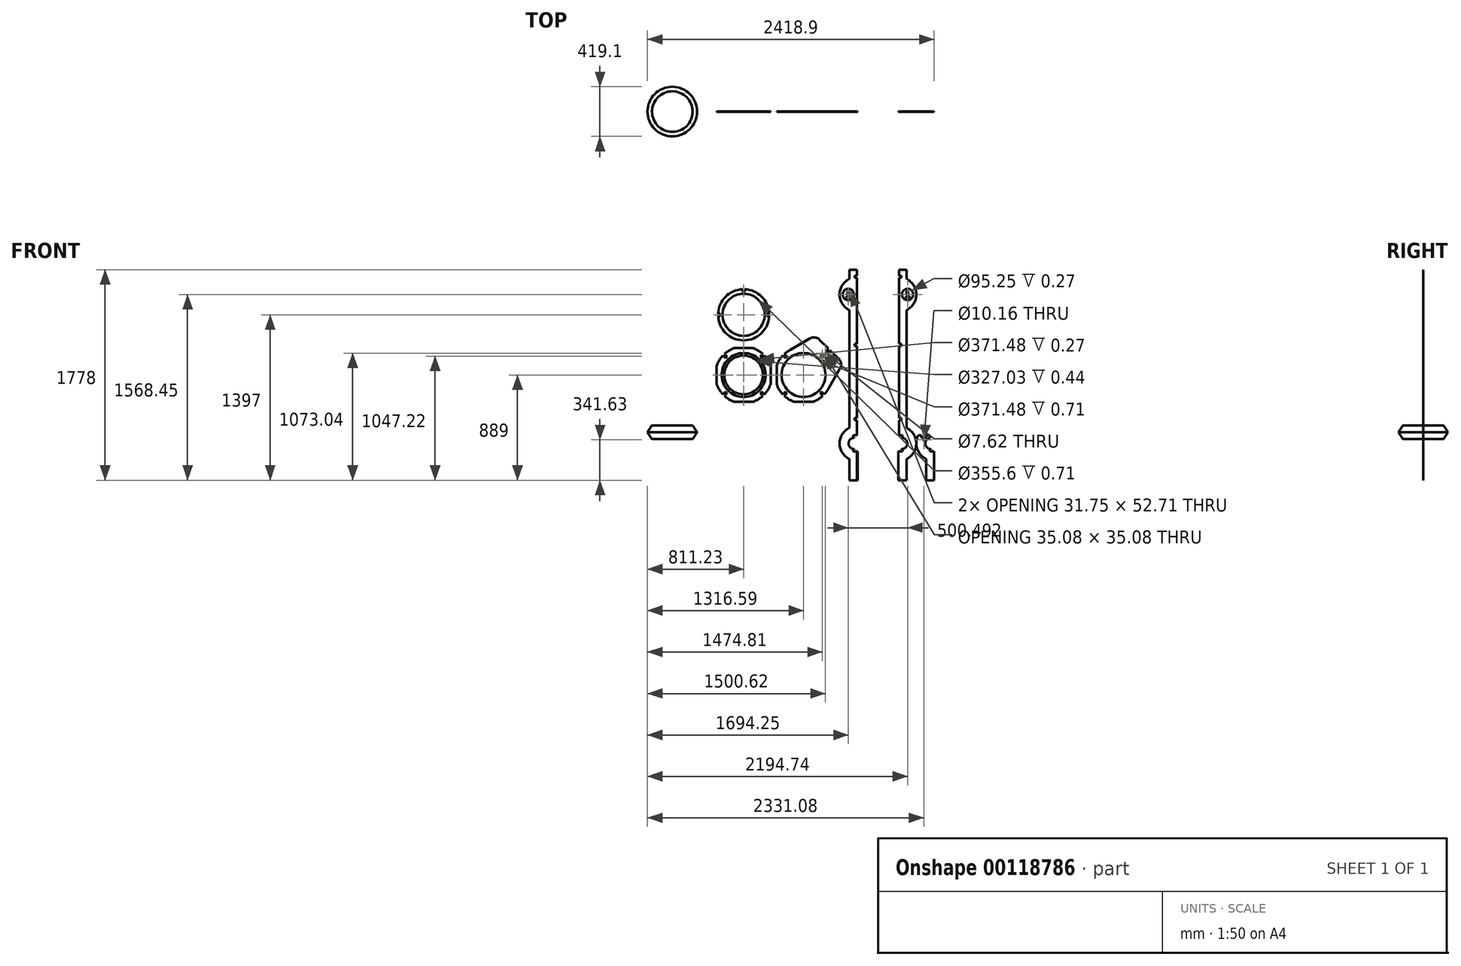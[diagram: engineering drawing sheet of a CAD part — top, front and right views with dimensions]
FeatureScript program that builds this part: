
annotation { "Feature Type Name" : "Feature", "Feature Type Description" : "" }
export const myFeature = defineFeature(function(context is Context, id is Id, definition is map)
    precondition{}
    {
        {
            assignVariable(context, id + "F0", {"name" : "thick", "anyValue" : 0.71});
        }
        {
            var Q0;
            Q0=qCreatedBy(makeId("Front.planeOp"),FACE);
            var sketch = newSketch(context, id + "F1", { "sketchPlane" : qUnion([Q0])});
            skArc(sketch, "E0", {"start": v(-76.2, 227.28) * mm, "mid": v(-169.5, 169.5) * mm, "end": v(-227.28, 76.2) * mm});
            skCircle(sketch, "E1.0", {"center": v(0, 0) * mm, "radius": 185.74 * mm});
            skCircle(sketch, "E2.0", {"center": v(0, 0) * mm, "radius": 163.51 * mm});
            skLineSegment(sketch, "E3", {"start": v(-169.5, 169.5) * mm, "end": v(169.5, -169.5) * mm, "construction": true});
            skLineSegment(sketch, "E4", {"start": v(0, 0) * mm, "end": v(-239.71, 0) * mm, "construction": true});
            skLineSegment(sketch, "E5.MirrorCS", {"start": v(-169.5, -169.5) * mm, "end": v(169.5, 169.5) * mm, "construction": true});
            skLineSegment(sketch, "E6.0", {"start": v(-163, 175.76) * mm, "end": v(-140.68, 153.43) * mm});
            skLineSegment(sketch, "E7.0", {"start": v(-175.76, 163) * mm, "end": v(-153.43, 140.68) * mm});
            skLineSegment(sketch, "E8", {"start": v(-140.68, 153.43) * mm, "end": v(-153.43, 140.68) * mm});
            skPoint(sketch, "E9", {"position": v(-147.05, 147.05) * mm});
            skLineSegment(sketch, "E10.1.0", {"start": v(-175.76, -163) * mm, "end": v(-153.43, -140.68) * mm});
            skLineSegment(sketch, "E10.1.1", {"start": v(-153.43, -140.68) * mm, "end": v(-140.68, -153.43) * mm});
            skLineSegment(sketch, "E10.1.2", {"start": v(-163, -175.76) * mm, "end": v(-140.68, -153.43) * mm});
            skLineSegment(sketch, "E10.2.0", {"start": v(163, -175.76) * mm, "end": v(140.68, -153.43) * mm});
            skLineSegment(sketch, "E10.2.1", {"start": v(140.68, -153.43) * mm, "end": v(153.43, -140.68) * mm});
            skLineSegment(sketch, "E10.2.2", {"start": v(175.76, -163) * mm, "end": v(153.43, -140.68) * mm});
            skLineSegment(sketch, "E10.3.0", {"start": v(175.76, 163) * mm, "end": v(153.43, 140.68) * mm});
            skLineSegment(sketch, "E10.3.1", {"start": v(153.43, 140.68) * mm, "end": v(140.68, 153.43) * mm});
            skLineSegment(sketch, "E10.3.2", {"start": v(163, 175.76) * mm, "end": v(140.68, 153.43) * mm});
            skLineSegment(sketch, "E11", {"start": v(-227.28, 76.2) * mm, "end": v(-227.28, -76.2) * mm});
            skLineSegment(sketch, "E12.1.0", {"start": v(-76.2, -227.28) * mm, "end": v(76.2, -227.28) * mm});
            skLineSegment(sketch, "E12.2.0", {"start": v(227.28, -76.2) * mm, "end": v(227.28, 76.2) * mm});
            skLineSegment(sketch, "E12.3.0", {"start": v(76.2, 227.28) * mm, "end": v(-76.2, 227.28) * mm});
            skArc(sketch, "E13.trimOffspring", {"start": v(227.28, 76.2) * mm, "mid": v(169.5, 169.5) * mm, "end": v(76.2, 227.28) * mm});
            skArc(sketch, "E14.trimOffspring", {"start": v(76.2, -227.28) * mm, "mid": v(169.5, -169.5) * mm, "end": v(227.28, -76.2) * mm});
            skArc(sketch, "E15.trimOffspring", {"start": v(-227.28, -76.2) * mm, "mid": v(-169.5, -169.5) * mm, "end": v(-76.2, -227.28) * mm});
            skLineSegment(sketch, "E16", {"start": v(252.68, 76.2) * mm, "end": v(252.68, -76.2) * mm, "construction": true});
            skLineSegment(sketch, "E17.MirrorCS", {"start": v(658.79, -140.68) * mm, "end": v(646.03, -153.43) * mm});
            skLineSegment(sketch, "E18.MirrorCS", {"start": v(646.03, 153.43) * mm, "end": v(658.79, 140.68) * mm});
            skPoint(sketch, "E19.MirrorP", {"position": v(505.36, 0) * mm});
            skLineSegment(sketch, "E20.MirrorCS", {"start": v(364.68, -153.43) * mm, "end": v(351.93, -140.68) * mm});
            skLineSegment(sketch, "E21.MirrorCS", {"start": v(351.93, 140.68) * mm, "end": v(364.68, 153.43) * mm});
            skLineSegment(sketch, "E22.MirrorCS", {"start": v(681.12, 163) * mm, "end": v(658.79, 140.68) * mm});
            skLineSegment(sketch, "E23.MirrorCS", {"start": v(342.35, 175.76) * mm, "end": v(364.68, 153.43) * mm});
            skLineSegment(sketch, "E24.MirrorCS", {"start": v(668.36, 175.76) * mm, "end": v(646.03, 153.43) * mm});
            skPoint(sketch, "E25.MirrorP", {"position": v(652.4, 147.05) * mm});
            skLineSegment(sketch, "E26.MirrorCS", {"start": v(581.56, -227.28) * mm, "end": v(429.16, -227.28) * mm});
            skArc(sketch, "E27.MirrorCS", {"start": v(278.08, 76.2) * mm, "mid": v(335.86, 169.5) * mm, "end": v(429.16, 227.28) * mm});
            skLineSegment(sketch, "E28.MirrorCS", {"start": v(681.12, -163) * mm, "end": v(658.79, -140.68) * mm});
            skLineSegment(sketch, "E29.MirrorCS", {"start": v(278.08, -76.2) * mm, "end": v(278.08, 76.2) * mm});
            skLineSegment(sketch, "E30.MirrorCS", {"start": v(674.86, -169.5) * mm, "end": v(335.86, 169.5) * mm, "construction": true});
            skArc(sketch, "E31.MirrorCS", {"start": v(732.64, -76.2) * mm, "mid": v(674.86, -169.5) * mm, "end": v(581.56, -227.28) * mm});
            skLineSegment(sketch, "E32.MirrorCS", {"start": v(329.6, -163) * mm, "end": v(351.93, -140.68) * mm});
            skLineSegment(sketch, "E33.MirrorCS", {"start": v(329.6, 163) * mm, "end": v(351.93, 140.68) * mm});
            skArc(sketch, "E34.MirrorCS", {"start": v(581.56, 227.28) * mm, "mid": v(674.86, 169.5) * mm, "end": v(732.64, 76.2) * mm});
            skLineSegment(sketch, "E35.MirrorCS", {"start": v(668.36, -175.76) * mm, "end": v(646.03, -153.43) * mm});
            skCircle(sketch, "E36.MirrorC", {"center": v(505.36, 0) * mm, "radius": 185.74 * mm});
            skLineSegment(sketch, "E37.MirrorCS", {"start": v(674.86, 169.5) * mm, "end": v(335.86, -169.5) * mm, "construction": true});
            skLineSegment(sketch, "E38.MirrorCS", {"start": v(505.36, 0) * mm, "end": v(745.07, 0) * mm, "construction": true});
            skLineSegment(sketch, "E39.MirrorCS", {"start": v(429.16, 227.28) * mm, "end": v(581.56, 227.28) * mm});
            skLineSegment(sketch, "E40.MirrorCS", {"start": v(732.64, 76.2) * mm, "end": v(732.64, -76.2) * mm});
            skCircle(sketch, "E41.MirrorC", {"center": v(505.36, 0) * mm, "radius": 163.51 * mm});
            skArc(sketch, "E42.MirrorCS", {"start": v(429.16, -227.28) * mm, "mid": v(335.86, -169.5) * mm, "end": v(278.08, -76.2) * mm});
            skLineSegment(sketch, "E43.MirrorCS", {"start": v(342.35, -175.76) * mm, "end": v(364.68, -153.43) * mm});
            skLineSegment(sketch, "E44", {"start": v(668.36, 175.76) * mm, "end": v(697.55, 204.94) * mm, "construction": true});
            skLineSegment(sketch, "E45", {"start": v(697.55, 204.94) * mm, "end": v(710.3, 192.2) * mm, "construction": true});
            skLineSegment(sketch, "E46", {"start": v(710.3, 192.2) * mm, "end": v(681.12, 163) * mm, "construction": true});
            skLineSegment(sketch, "E47", {"start": v(581.56, 227.28) * mm, "end": v(674.27, 227.28) * mm, "construction": true});
            skLineSegment(sketch, "E48", {"start": v(732.64, 76.2) * mm, "end": v(732.64, 168.91) * mm, "construction": true});
            skPoint(sketch, "E49", {"position": v(703.93, 198.57) * mm});
            skCircle(sketch, "E50", {"center": v(0, 508) * mm, "radius": 228.3 * mm, "construction": true});
            skPoint(sketch, "E50.centerSnap0", {"position": v(0, 227.28) * mm});
            skCircle(sketch, "E51.0", {"center": v(0, 508) * mm, "radius": 215.9 * mm});
            skCircle(sketch, "E52.0", {"center": v(0, 508) * mm, "radius": 177.8 * mm});
            skLineSegment(sketch, "E53.bottom", {"start": v(9.02, 723.71) * mm, "end": v(-9.02, 723.71) * mm});
            skLineSegment(sketch, "E53.top", {"start": v(9.02, 704.66) * mm, "end": v(-9.02, 704.66) * mm});
            skLineSegment(sketch, "E53.left", {"start": v(9.02, 723.71) * mm, "end": v(9.02, 704.66) * mm});
            skLineSegment(sketch, "E53.right", {"start": v(-9.02, 723.71) * mm, "end": v(-9.02, 704.66) * mm});
            skPoint(sketch, "E53.middle", {"position": v(0, 714.19) * mm});
            skLineSegment(sketch, "E54.1.0", {"start": v(-215.71, 498.98) * mm, "end": v(-196.66, 498.98) * mm});
            skLineSegment(sketch, "E54.1.1", {"start": v(-215.71, 517.02) * mm, "end": v(-196.66, 517.02) * mm});
            skLineSegment(sketch, "E54.1.2", {"start": v(-196.66, 517.02) * mm, "end": v(-196.66, 498.98) * mm});
            skLineSegment(sketch, "E54.2.0", {"start": v(9.02, 292.29) * mm, "end": v(9.02, 311.34) * mm, "construction": true});
            skLineSegment(sketch, "E54.2.1", {"start": v(-9.02, 292.29) * mm, "end": v(-9.02, 311.34) * mm, "construction": true});
            skLineSegment(sketch, "E54.2.2", {"start": v(-9.02, 311.34) * mm, "end": v(9.02, 311.34) * mm, "construction": true});
            skLineSegment(sketch, "E54.3.0", {"start": v(215.71, 517.02) * mm, "end": v(196.66, 517.02) * mm});
            skLineSegment(sketch, "E54.3.1", {"start": v(215.71, 498.98) * mm, "end": v(196.66, 498.98) * mm});
            skLineSegment(sketch, "E54.3.2", {"start": v(196.66, 498.98) * mm, "end": v(196.66, 517.02) * mm});
            skLineSegment(sketch, "E55.bottom", {"start": v(1310.49, 889) * mm, "end": v(1373.99, 889) * mm});
            skLineSegment(sketch, "E55.top", {"start": v(1310.49, -889) * mm, "end": v(1373.99, -889) * mm});
            skLineSegment(sketch, "E55.left", {"start": v(1310.49, 889) * mm, "end": v(1310.49, -487.93) * mm});
            skLineSegment(sketch, "E55.right", {"start": v(1373.99, 889) * mm, "end": v(1373.99, 810.97) * mm});
            skPoint(sketch, "E55.middle", {"position": v(1342.24, 0) * mm});
            skArc(sketch, "E56", {"start": v(1310.49, -628.65) * mm, "mid": v(1380.84, -558.3) * mm, "end": v(1310.49, -487.93) * mm, "construction": true});
            skArc(sketch, "E57.0", {"start": v(1373.99, -709.37) * mm, "mid": v(1456.54, -577.85) * mm, "end": v(1373.99, -446.33) * mm});
            skLineSegment(sketch, "E58.trimOffspring", {"start": v(1310.49, -628.65) * mm, "end": v(1310.49, -889) * mm});
            skLineSegment(sketch, "E59.trimOffspring", {"start": v(1373.99, -709.37) * mm, "end": v(1373.99, -889) * mm});
            skArc(sketch, "E60", {"start": v(1373.99, 547.93) * mm, "mid": v(1456.54, 679.45) * mm, "end": v(1373.99, 810.97) * mm});
            skLineSegment(sketch, "E61.trimOffspring", {"start": v(1373.99, 547.93) * mm, "end": v(1373.99, -446.33) * mm});
            skCircle(sketch, "E62", {"center": v(1383.51, 679.45) * mm, "radius": 47.63 * mm});
            skLineSegment(sketch, "E63", {"start": v(1310.49, 679.45) * mm, "end": v(1456.54, 679.45) * mm, "construction": true});
            skLineSegment(sketch, "E64.bottom", {"start": v(1387.64, 705.8) * mm, "end": v(1379.38, 705.8) * mm});
            skLineSegment(sketch, "E64.top", {"start": v(1387.64, 661.35) * mm, "end": v(1379.38, 661.35) * mm});
            skLineSegment(sketch, "E64.left", {"start": v(1387.64, 705.8) * mm, "end": v(1387.64, 661.35) * mm});
            skLineSegment(sketch, "E64.right", {"start": v(1379.38, 705.8) * mm, "end": v(1379.38, 661.35) * mm});
            skLineSegment(sketch, "E65.bottom", {"start": v(1367.64, 661.35) * mm, "end": v(1399.39, 661.35) * mm});
            skLineSegment(sketch, "E65.top", {"start": v(1367.64, 653.1) * mm, "end": v(1399.39, 653.1) * mm});
            skLineSegment(sketch, "E65.left", {"start": v(1367.64, 661.35) * mm, "end": v(1367.64, 653.1) * mm});
            skLineSegment(sketch, "E65.right", {"start": v(1399.39, 661.35) * mm, "end": v(1399.39, 653.1) * mm});
            skPoint(sketch, "E65.middle", {"position": v(1383.51, 657.22) * mm});
            skPoint(sketch, "E65.middle.positionSnap0", {"position": v(1383.51, 661.35) * mm});
            skPoint(sketch, "E65.cornerSnap0", {"position": v(1383.51, 661.35) * mm});
            skPoint(sketch, "E65.centerSnap0", {"position": v(1383.51, 661.35) * mm});
            skLineSegment(sketch, "E66", {"start": v(1379.38, 705.8) * mm, "end": v(1367.64, 693.74) * mm});
            skLineSegment(sketch, "E67", {"start": v(1367.64, 693.74) * mm, "end": v(1373.55, 687.98) * mm});
            skLineSegment(sketch, "E68", {"start": v(1373.55, 687.98) * mm, "end": v(1379.38, 693.97) * mm});
            skLineSegment(sketch, "E69", {"start": v(1383.51, 705.8) * mm, "end": v(1383.51, 653.1) * mm, "construction": true});
            skLineSegment(sketch, "E70.left", {"start": v(1310.49, -646.68) * mm, "end": v(1310.49, -628.65) * mm});
            skLineSegment(sketch, "E70.right", {"start": v(1340.84, -646.68) * mm, "end": v(1340.84, -628.65) * mm});
            skLineSegment(sketch, "E71", {"start": v(1310.49, -558.3) * mm, "end": v(1380.84, -558.3) * mm, "construction": true});
            skLineSegment(sketch, "E72.bottom", {"start": v(1310.49, 838.2) * mm, "end": v(1329.54, 838.2) * mm});
            skLineSegment(sketch, "E72.top", {"start": v(1310.49, 820.17) * mm, "end": v(1329.54, 820.17) * mm});
            skLineSegment(sketch, "E72.left", {"start": v(1310.49, 838.2) * mm, "end": v(1310.49, 820.17) * mm});
            skLineSegment(sketch, "E72.right", {"start": v(1329.54, 838.2) * mm, "end": v(1329.54, 820.17) * mm});
            skLineSegment(sketch, "E73.bottom", {"start": v(1310.49, 263.02) * mm, "end": v(1329.54, 263.02) * mm});
            skLineSegment(sketch, "E73.top", {"start": v(1310.49, 244.98) * mm, "end": v(1329.54, 244.98) * mm});
            skLineSegment(sketch, "E73.left", {"start": v(1310.49, 263.02) * mm, "end": v(1310.49, 244.98) * mm});
            skLineSegment(sketch, "E73.right", {"start": v(1329.54, 263.02) * mm, "end": v(1329.54, 244.98) * mm});
            skLineSegment(sketch, "E74.bottom", {"start": v(1310.49, -362.97) * mm, "end": v(1329.54, -362.97) * mm});
            skLineSegment(sketch, "E74.top", {"start": v(1310.49, -381) * mm, "end": v(1329.54, -381) * mm});
            skLineSegment(sketch, "E74.left", {"start": v(1310.49, -362.97) * mm, "end": v(1310.49, -381) * mm});
            skLineSegment(sketch, "E74.right", {"start": v(1329.54, -362.97) * mm, "end": v(1329.54, -381) * mm});
            skLineSegment(sketch, "E75", {"start": v(1133.27, 889) * mm, "end": v(1133.27, -381) * mm, "construction": true});
            skLineSegment(sketch, "E76", {"start": v(1133.27, 254) * mm, "end": v(1329.54, 254) * mm, "construction": true});
            skCircle(sketch, "E77.MirrorC", {"center": v(883.02, 679.45) * mm, "radius": 47.63 * mm});
            skLineSegment(sketch, "E78.MirrorCS", {"start": v(956.04, 838.2) * mm, "end": v(937, 838.2) * mm});
            skLineSegment(sketch, "E79.MirrorCS", {"start": v(956.04, 244.98) * mm, "end": v(937, 244.98) * mm});
            skLineSegment(sketch, "E80.MirrorCS", {"start": v(937, 263.02) * mm, "end": v(937, 244.98) * mm});
            skLineSegment(sketch, "E81.MirrorCS", {"start": v(956.04, 263.02) * mm, "end": v(956.04, 244.98) * mm});
            skLineSegment(sketch, "E82.MirrorCS", {"start": v(956.04, 820.17) * mm, "end": v(937, 820.17) * mm});
            skLineSegment(sketch, "E83.MirrorCS", {"start": v(956.04, 838.2) * mm, "end": v(956.04, 820.17) * mm});
            skLineSegment(sketch, "E84.MirrorCS", {"start": v(956.04, -362.97) * mm, "end": v(937, -362.97) * mm});
            skLineSegment(sketch, "E85.MirrorCS", {"start": v(937, 838.2) * mm, "end": v(937, 820.17) * mm});
            skLineSegment(sketch, "E86.MirrorCS", {"start": v(956.04, 263.02) * mm, "end": v(937, 263.02) * mm});
            skLineSegment(sketch, "E87.MirrorCS", {"start": v(892.54, 889) * mm, "end": v(892.54, 810.97) * mm});
            skLineSegment(sketch, "E88.MirrorCS", {"start": v(956.04, -381) * mm, "end": v(937, -381) * mm});
            skLineSegment(sketch, "E89.MirrorCS", {"start": v(956.04, -889) * mm, "end": v(892.54, -889) * mm});
            skLineSegment(sketch, "E90.MirrorCS", {"start": v(956.04, -362.97) * mm, "end": v(956.04, -381) * mm});
            skLineSegment(sketch, "E91.MirrorCS", {"start": v(937, -362.97) * mm, "end": v(937, -381) * mm});
            skLineSegment(sketch, "E92.MirrorCS", {"start": v(956.04, 889) * mm, "end": v(892.54, 889) * mm});
            skLineSegment(sketch, "E93.MirrorCS", {"start": v(956.04, 679.45) * mm, "end": v(810, 679.45) * mm, "construction": true});
            skArc(sketch, "E94.MirrorCS", {"start": v(956.04, -628.65) * mm, "mid": v(885.69, -558.3) * mm, "end": v(956.04, -487.93) * mm, "construction": true});
            skLineSegment(sketch, "E95.MirrorCS", {"start": v(956.04, -558.3) * mm, "end": v(885.69, -558.3) * mm, "construction": true});
            skLineSegment(sketch, "E96.MirrorCS", {"start": v(892.54, 547.93) * mm, "end": v(892.54, -446.33) * mm});
            skPoint(sketch, "E97.MirrorP", {"position": v(924.3, 0) * mm});
            skArc(sketch, "E98.MirrorCS", {"start": v(892.54, 547.93) * mm, "mid": v(810, 679.45) * mm, "end": v(892.54, 810.97) * mm});
            skArc(sketch, "E99.MirrorCS", {"start": v(892.54, -709.37) * mm, "mid": v(810, -577.85) * mm, "end": v(892.54, -446.33) * mm});
            skLineSegment(sketch, "E100.MirrorCS", {"start": v(892.54, -709.37) * mm, "end": v(892.54, -889) * mm});
            skLineSegment(sketch, "E101.MirrorCS", {"start": v(956.04, 889) * mm, "end": v(956.04, -487.93) * mm});
            skLineSegment(sketch, "E102.MirrorCS", {"start": v(956.04, -628.65) * mm, "end": v(956.04, -889) * mm});
            skLineSegment(sketch, "E103.bottom", {"start": v(887.15, 705.8) * mm, "end": v(878.9, 705.8) * mm});
            skLineSegment(sketch, "E103.top", {"start": v(887.15, 661.35) * mm, "end": v(878.9, 661.35) * mm});
            skLineSegment(sketch, "E103.left", {"start": v(887.15, 705.8) * mm, "end": v(887.15, 661.35) * mm});
            skLineSegment(sketch, "E103.right", {"start": v(878.9, 705.8) * mm, "end": v(878.9, 661.35) * mm});
            skLineSegment(sketch, "E104.bottom", {"start": v(867.14, 661.35) * mm, "end": v(898.9, 661.35) * mm});
            skLineSegment(sketch, "E104.top", {"start": v(867.14, 653.1) * mm, "end": v(898.9, 653.1) * mm});
            skLineSegment(sketch, "E104.left", {"start": v(867.14, 661.35) * mm, "end": v(867.14, 653.1) * mm});
            skLineSegment(sketch, "E104.right", {"start": v(898.9, 661.35) * mm, "end": v(898.9, 653.1) * mm});
            skPoint(sketch, "E104.middle", {"position": v(883.02, 657.22) * mm});
            skPoint(sketch, "E104.middle.positionSnap0", {"position": v(883.02, 661.35) * mm});
            skPoint(sketch, "E104.cornerSnap0", {"position": v(883.02, 661.35) * mm});
            skPoint(sketch, "E104.centerSnap0", {"position": v(883.02, 661.35) * mm});
            skLineSegment(sketch, "E105", {"start": v(878.9, 705.8) * mm, "end": v(867.14, 693.74) * mm});
            skLineSegment(sketch, "E106", {"start": v(867.14, 693.74) * mm, "end": v(873.06, 687.98) * mm});
            skLineSegment(sketch, "E107", {"start": v(873.06, 687.98) * mm, "end": v(878.9, 693.97) * mm});
            skLineSegment(sketch, "E108", {"start": v(883.02, 705.8) * mm, "end": v(883.02, 653.1) * mm, "construction": true});
            skArc(sketch, "E109", {"start": v(697.55, 204.94) * mm, "mid": v(686.03, 216.23) * mm, "end": v(674.27, 227.28) * mm, "construction": true});
            skArc(sketch, "E110.MirrorCS", {"start": v(710.3, 192.2) * mm, "mid": v(721.59, 180.67) * mm, "end": v(732.64, 168.91) * mm, "construction": true});
            skLineSegment(sketch, "E111", {"start": v(-169.5, 169.5) * mm, "end": v(-163.13, 175.88) * mm});
            skLineSegment(sketch, "E112.0", {"start": v(-220.9, 220.9) * mm, "end": v(-214.53, 227.28) * mm, "construction": true});
            skLineSegment(sketch, "E113", {"start": v(-76.2, 227.28) * mm, "end": v(-214.53, 227.28) * mm, "construction": true});
            skPoint(sketch, "E114", {"position": v(1456.54, -577.85) * mm});
            skLineSegment(sketch, "E115", {"start": v(-220.9, 220.9) * mm, "end": v(-147.05, 147.05) * mm, "construction": true});
            skLineSegment(sketch, "E116", {"start": v(1456.54, 679.45) * mm, "end": v(1456.54, -577.85) * mm, "construction": true});
            skLineSegment(sketch, "E117", {"start": v(892.54, -889) * mm, "end": v(961.12, -889) * mm});
            skPoint(sketch, "E117.endSnap0", {"position": v(924.3, -889) * mm});
            skLineSegment(sketch, "E118", {"start": v(961.12, -889) * mm, "end": v(961.12, -646.68) * mm});
            skLineSegment(sketch, "E119", {"start": v(961.12, -646.68) * mm, "end": v(956.04, -646.68) * mm});
            skLineSegment(sketch, "E120.MirrorCS", {"start": v(1305.4, -889) * mm, "end": v(1305.4, -646.68) * mm});
            skLineSegment(sketch, "E121.MirrorCS", {"start": v(1305.4, -646.68) * mm, "end": v(1310.49, -646.68) * mm});
            skLineSegment(sketch, "E122", {"start": v(-241.11, 498.98) * mm, "end": v(-241.11, 517.02) * mm, "construction": true});
            skLineSegment(sketch, "E123", {"start": v(1305.4, -889) * mm, "end": v(1310.49, -889) * mm});
            skLineSegment(sketch, "E124", {"start": v(1340.84, -628.65) * mm, "end": v(1331.7, -628.65) * mm});
            skLineSegment(sketch, "E125", {"start": v(1331.7, -628.65) * mm, "end": v(1331.7, -626.07) * mm});
            skLineSegment(sketch, "E126", {"start": v(1380.84, -520.2) * mm, "end": v(1380.84, -596.4) * mm, "construction": true});
            skPoint(sketch, "E127", {"position": v(1380.84, -558.3) * mm});
            skLineSegment(sketch, "E128", {"start": v(1340.84, -646.68) * mm, "end": v(1310.49, -646.68) * mm});
            skLineSegment(sketch, "E129", {"start": v(1310.49, -577.85) * mm, "end": v(1380.84, -577.85) * mm, "construction": true});
            skLineSegment(sketch, "E130.MirrorCS", {"start": v(1331.7, -527.05) * mm, "end": v(1331.7, -529.63) * mm});
            skLineSegment(sketch, "E131.MirrorCS", {"start": v(1340.84, -527.05) * mm, "end": v(1331.7, -527.05) * mm});
            skArc(sketch, "E132", {"start": v(1331.7, -626.07) * mm, "mid": v(1380.84, -577.85) * mm, "end": v(1331.7, -529.63) * mm});
            skLineSegment(sketch, "E133.MirrorCS", {"start": v(1340.84, -509.02) * mm, "end": v(1340.84, -527.05) * mm});
            skLineSegment(sketch, "E134.MirrorCS", {"start": v(1340.84, -509.02) * mm, "end": v(1310.49, -509.02) * mm});
            skLineSegment(sketch, "E135", {"start": v(1310.49, -487.93) * mm, "end": v(1310.49, -509.02) * mm});
            skLineSegment(sketch, "E136.MirrorCS", {"start": v(925.7, -646.68) * mm, "end": v(956.04, -646.68) * mm});
            skLineSegment(sketch, "E137.MirrorCS", {"start": v(925.7, -628.65) * mm, "end": v(934.83, -628.65) * mm});
            skLineSegment(sketch, "E138.MirrorCS", {"start": v(925.7, -646.68) * mm, "end": v(925.7, -628.65) * mm});
            skLineSegment(sketch, "E139.MirrorCS", {"start": v(934.83, -628.65) * mm, "end": v(934.83, -626.07) * mm});
            skArc(sketch, "E140.MirrorCS", {"start": v(934.83, -626.07) * mm, "mid": v(885.69, -577.85) * mm, "end": v(934.83, -529.63) * mm});
            skLineSegment(sketch, "E141.MirrorCS", {"start": v(934.83, -527.05) * mm, "end": v(934.83, -529.63) * mm});
            skLineSegment(sketch, "E142.MirrorCS", {"start": v(925.7, -527.05) * mm, "end": v(934.83, -527.05) * mm});
            skLineSegment(sketch, "E143.MirrorCS", {"start": v(925.7, -509.02) * mm, "end": v(925.7, -527.05) * mm});
            skLineSegment(sketch, "E144.MirrorCS", {"start": v(925.7, -509.02) * mm, "end": v(956.04, -509.02) * mm});
            skLineSegment(sketch, "E145.MirrorCS", {"start": v(956.04, -487.93) * mm, "end": v(956.04, -509.02) * mm});
            skLineSegment(sketch, "E146", {"start": v(639.61, 299.04) * mm, "end": v(722, 216.65) * mm});
            skLineSegment(sketch, "E147", {"start": v(703.93, 198.57) * mm, "end": v(722, 216.65) * mm, "construction": true});
            skLineSegment(sketch, "E148.MirrorCS", {"start": v(838.75, 99.9) * mm, "end": v(722, 216.65) * mm});
            skLineSegment(sketch, "E149", {"start": v(394.72, 212.66) * mm, "end": v(563.12, 309.23) * mm});
            skLineSegment(sketch, "E150.MirrorCS", {"start": v(718.01, -110.63) * mm, "end": v(838.75, 99.9) * mm});
            skPoint(sketch, "E151.visualSharp", {"position": v(605.26, 333.4) * mm});
            skArc(sketch, "E151.filletArc", {"start": v(639.61, 299.04) * mm, "mid": v(603.1, 317.09) * mm, "end": v(563.12, 309.23) * mm});
            skArc(sketch, "E152.MirrorCS", {"start": v(804.4, 134.26) * mm, "mid": v(822.44, 97.73) * mm, "end": v(814.58, 57.76) * mm});
            skLineSegment(sketch, "E153", {"start": v(697.55, 204.94) * mm, "end": v(715.63, 223.02) * mm});
            skLineSegment(sketch, "E154", {"start": v(697.55, 204.94) * mm, "end": v(710.3, 192.2) * mm});
            skLineSegment(sketch, "E155", {"start": v(710.3, 192.2) * mm, "end": v(728.38, 210.27) * mm});
            skLineSegment(sketch, "E156", {"start": v(728.38, 210.27) * mm, "end": v(715.63, 223.02) * mm});
            skLineSegment(sketch, "E157.MirrorCS", {"start": v(1572.24, -509.02) * mm, "end": v(1572.24, -527.05) * mm});
            skLineSegment(sketch, "E158.MirrorCS", {"start": v(1572.24, -527.05) * mm, "end": v(1581.37, -527.05) * mm});
            skLineSegment(sketch, "E159.MirrorCS", {"start": v(1581.37, -527.05) * mm, "end": v(1581.37, -529.63) * mm});
            skArc(sketch, "E160.MirrorCS", {"start": v(1581.37, -626.07) * mm, "mid": v(1532.23, -577.85) * mm, "end": v(1581.37, -529.63) * mm});
            skLineSegment(sketch, "E161.MirrorCS", {"start": v(1581.37, -628.65) * mm, "end": v(1581.37, -626.07) * mm});
            skLineSegment(sketch, "E162.MirrorCS", {"start": v(1572.24, -628.65) * mm, "end": v(1581.37, -628.65) * mm});
            skLineSegment(sketch, "E163.MirrorCS", {"start": v(1572.24, -646.68) * mm, "end": v(1572.24, -628.65) * mm});
            skLineSegment(sketch, "E164.MirrorCS", {"start": v(1572.24, -646.68) * mm, "end": v(1602.59, -646.68) * mm});
            skLineSegment(sketch, "E165.MirrorCS", {"start": v(1607.67, -889) * mm, "end": v(1607.67, -646.68) * mm});
            skLineSegment(sketch, "E166.MirrorCS", {"start": v(1607.67, -646.68) * mm, "end": v(1602.59, -646.68) * mm});
            skLineSegment(sketch, "E167.MirrorCS", {"start": v(1602.59, -889) * mm, "end": v(1539.09, -889) * mm});
            skLineSegment(sketch, "E168.MirrorCS", {"start": v(1539.09, -709.37) * mm, "end": v(1539.09, -889) * mm});
            skArc(sketch, "E169.MirrorCS", {"start": v(1539.09, -709.37) * mm, "mid": v(1463.73, -623.11) * mm, "end": v(1473.77, -509.02) * mm});
            skLineSegment(sketch, "E170", {"start": v(1572.24, -509.02) * mm, "end": v(1540.49, -509.02) * mm});
            skLineSegment(sketch, "E171", {"start": v(1540.49, -509.02) * mm, "end": v(1540.49, -527.05) * mm});
            skLineSegment(sketch, "E172", {"start": v(1540.49, -527.05) * mm, "end": v(1499.21, -527.05) * mm});
            skLineSegment(sketch, "E173", {"start": v(1499.21, -527.05) * mm, "end": v(1499.21, -509.02) * mm});
            skLineSegment(sketch, "E174", {"start": v(1499.21, -509.02) * mm, "end": v(1473.77, -509.02) * mm});
            skPoint(sketch, "E175.orphan", {"position": v(1539.09, -446.33) * mm});
            skLineSegment(sketch, "E176", {"start": v(1572.24, -527.05) * mm, "end": v(1572.24, -530.33) * mm});
            skLineSegment(sketch, "E177", {"start": v(1602.59, -889) * mm, "end": v(1607.67, -889) * mm});
            skCircle(sketch, "E178", {"center": v(1519.85, -547.37) * mm, "radius": 5.08 * mm});
            skPoint(sketch, "E178.centerSnap0", {"position": v(1519.85, -527.05) * mm});
            skLineSegment(sketch, "E179", {"start": v(674.86, 169.5) * mm, "end": v(703.93, 198.57) * mm, "construction": true});
            skCircle(sketch, "E180", {"center": v(689.4, 184.04) * mm, "radius": 3.81 * mm});
            skLineSegment(sketch, "E181.bottom", {"start": v(-773.13, -426.71) * mm, "end": v(-430.23, -426.71) * mm});
            skLineSegment(sketch, "E181.top", {"start": v(-773.13, -541.01) * mm, "end": v(-430.23, -541.01) * mm});
            skLineSegment(sketch, "E181.left", {"start": v(-773.13, -426.71) * mm, "end": v(-773.13, -541.01) * mm});
            skLineSegment(sketch, "E181.right", {"start": v(-430.23, -426.71) * mm, "end": v(-430.23, -541.01) * mm});
            skLineSegment(sketch, "E182", {"start": v(-773.13, -426.71) * mm, "end": v(-811.23, -483.86) * mm});
            skPoint(sketch, "E182.endSnap0", {"position": v(-773.13, -483.86) * mm});
            skLineSegment(sketch, "E183", {"start": v(-811.23, -483.86) * mm, "end": v(-773.13, -541.01) * mm});
            skLineSegment(sketch, "E184", {"start": v(-430.23, -426.71) * mm, "end": v(-392.13, -483.86) * mm});
            skPoint(sketch, "E184.endSnap0", {"position": v(-430.23, -483.86) * mm});
            skLineSegment(sketch, "E185", {"start": v(-392.13, -483.86) * mm, "end": v(-430.23, -541.01) * mm});
            skLineSegment(sketch, "E186", {"start": v(-601.68, -426.71) * mm, "end": v(-601.68, -541.01) * mm});
            skSolve(sketch);
        }
        {
            var Q0;
            Q0=makeQuery(id+"F1.imprint","IMPRINT",FACE,{"disambiguationData":[TD([[makeQuery(id+"F1.imprint","IMPRINT",EDGE,{"derivedFrom":sQuery(id+"F1.wireOp",EDGE,"E52.0")}),-1.0]])]});
            var Q1;
            Q1=makeQuery(id+"F1.imprint","IMPRINT",FACE,{"disambiguationData":[TD([[makeQuery(id+"F1.imprint","IMPRINT",EDGE,{"derivedFrom":sQuery(id+"F1.wireOp",EDGE,"E1.0")}),-1.0]])]});
            var Q2;
            Q2=makeQuery(id+"F1.imprint","IMPRINT",FACE,{"disambiguationData":[TD([[makeQuery(id+"F1.imprint","IMPRINT",EDGE,{"derivedFrom":sQuery(id+"F1.wireOp",EDGE,"E17.MirrorCS")}),-1.0]])]});
            var Q3;
            {var subQ12=sQuery(id+"F1.wireOp",EDGE,"ca3a832c-03f7-4a1b-8a6c-0b75b93ac6f213.MirrorCS");Q3=makeQuery(id+"F1.imprint","IMPRINT",FACE,{"disambiguationData":[TD([[makeQuery(id+"F1.imprint","IMPRINT",EDGE,{"derivedFrom":subQ12}),1.0]])]});}
            var Q4;
            {var subQ16=sQuery(id+"F1.wireOp",EDGE,"E55.bottom");Q4=makeQuery(id+"F1.imprint","IMPRINT",FACE,{"disambiguationData":[TD([[makeQuery(id+"F1.imprint","IMPRINT",EDGE,{"derivedFrom":subQ16}),-1.0]])]});}
            var Q5;
            {var subQ4=sQuery(id+"F1.wireOp",EDGE,"E39.MirrorCS");Q5=makeQuery(id+"F1.imprint","IMPRINT",FACE,{"disambiguationData":[TD([[makeQuery(id+"F1.imprint","IMPRINT",EDGE,{"derivedFrom":subQ4}),1.0]])]});}
            var Q6;
            Q6=makeQuery(id+"F1.imprint","IMPRINT",FACE,{"disambiguationData":[TD([[makeQuery(id+"F1.imprint","IMPRINT",EDGE,{"derivedFrom":sQuery(id+"F1.wireOp",EDGE,"E77.MirrorC")}),1.0]])]});
            var Q7;
            Q7=makeQuery(id+"F1.imprint","IMPRINT",FACE,{"disambiguationData":[TD([[makeQuery(id+"F1.imprint","IMPRINT",EDGE,{"derivedFrom":sQuery(id+"F1.wireOp",EDGE,"E157.MirrorCS")}),-1.0]])]});
            var Q8;
            {var subQ4=sQuery(id+"F1.wireOp",EDGE,"E118");Q8=makeQuery(id+"F1.imprint","IMPRINT",FACE,{"disambiguationData":[TD([[makeQuery(id+"F1.imprint","IMPRINT",EDGE,{"derivedFrom":subQ4}),1.0]])]});}
            var Q9;
            Q9=makeQuery(id+"F1.imprint","IMPRINT",FACE,{"disambiguationData":[TD([[makeQuery(id+"F1.imprint","IMPRINT",EDGE,{"derivedFrom":sQuery(id+"F1.wireOp",EDGE,"E58.trimOffspring")}),-1.0]])]});
            extrude(context, id + "F2", {"entities" : qUnion([Q0, Q1, Q2, Q3, Q4, Q5, Q6, Q7, Q8, Q9]), "depth" : (getVariable(context, 'thick')) * mm});
        }
        {
            var Q0;
            Q0=makeQuery(id+"F1.imprint","IMPRINT",FACE,{"disambiguationData":[TD([[makeQuery(id+"F1.imprint","IMPRINT",EDGE,{"derivedFrom":sQuery(id+"F1.wireOp",EDGE,"E1.0")}),1.0]])]});
            var Q1;
            Q1=makeQuery(id+"F1.imprint","IMPRINT",FACE,{"disambiguationData":[TD([[makeQuery(id+"F1.imprint","IMPRINT",EDGE,{"derivedFrom":sQuery(id+"F1.wireOp",EDGE,"E36.MirrorC")}),-1.0]])]});
            var Q2;
            Q2=makeQuery(id+"F1.imprint","IMPRINT",FACE,{"disambiguationData":[TD([[makeQuery(id+"F1.imprint","IMPRINT",EDGE,{"derivedFrom":sQuery(id+"F1.wireOp",EDGE,"ca3a832c-03f7-4a1b-8a6c-0b75b93ac6f22.MirrorCS")}),1.0]])]});
            var Q3;
            Q3=makeQuery(id+"F1.imprint","IMPRINT",FACE,{"disambiguationData":[TD([[makeQuery(id+"F1.imprint","IMPRINT",EDGE,{"derivedFrom":sQuery(id+"F1.wireOp",EDGE,"E62")}),1.0]])]});
            var Q4;
            Q4=makeQuery(id+"F1.imprint","IMPRINT",FACE,{"disambiguationData":[TD([[makeQuery(id+"F1.imprint","IMPRINT",EDGE,{"derivedFrom":sQuery(id+"F1.wireOp",EDGE,"E77.MirrorC")}),-1.0]])]});
            extrude(context, id + "F3", {"entities" : qUnion([Q0, Q1, Q2, Q3, Q4]), "operationType" : NewBodyOperationType.ADD, "depth" : (getVariable(context, 'thick') - .27) * mm});
        }
        {
            var Q0;
            {var subQ0=sQuery(id+"F1.wireOp",EDGE,"E181.right");Q0=makeQuery(id+"F1.imprint","IMPRINT",FACE,{"disambiguationData":[TD([[makeQuery(id+"F1.imprint","IMPRINT",EDGE,{"derivedFrom":subQ0}),-1.0]])]});}
            var Q1;
            Q1=makeQuery(id+"F1.imprint","IMPRINT",FACE,{"disambiguationData":[TD([[makeQuery(id+"F1.imprint","IMPRINT",EDGE,{"derivedFrom":sQuery(id+"F1.wireOp",EDGE,"E181.right")}),1.0]])]});
            var Q2;
            Q2=sQuery(id+"F1.wireOp",EDGE,"E186");
            revolve(context, id + "F4", {"entities" : qUnion([Q0, Q1]), "axis" : qUnion([Q2]), "revolveType" : RevolveType.FULL});
        }
    });
